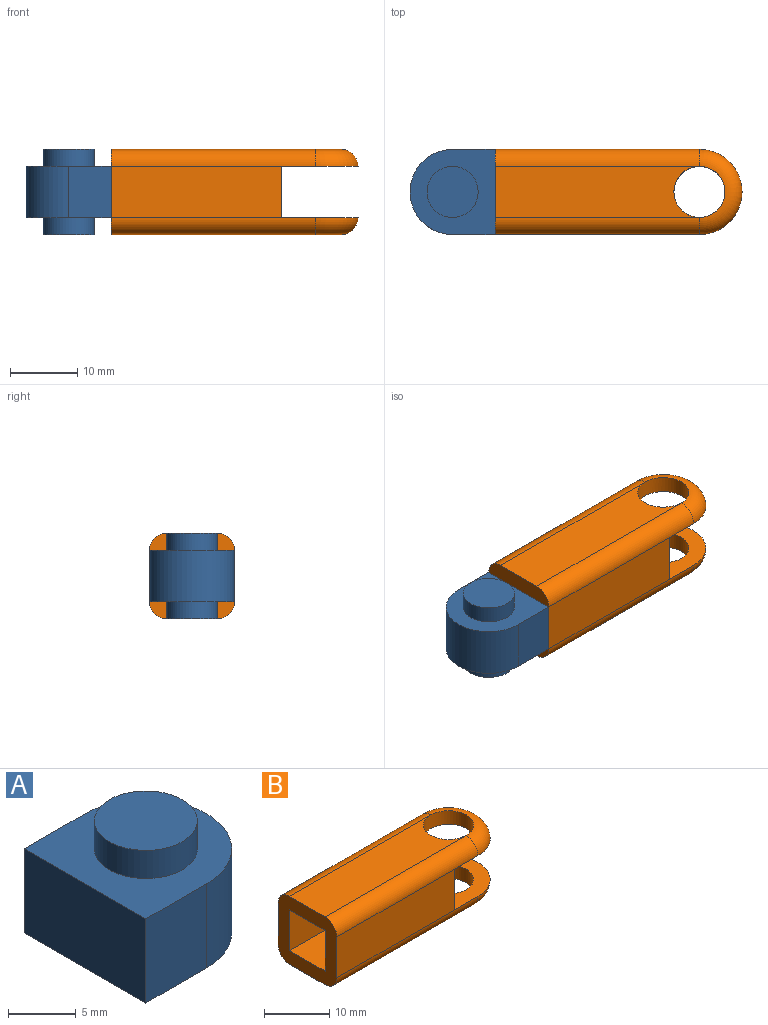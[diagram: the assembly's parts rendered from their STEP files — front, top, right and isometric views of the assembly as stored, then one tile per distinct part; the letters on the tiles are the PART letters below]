
ASSEMBLY  parts=2 mates=1
PART A: 10 faces, bbox 12.7x12.7x12.7 mm
  f0: cylinder r=6.35mm len=12.7mm, axis (0,0,-1), area 152mm2, adj f1,f3,f4,f5
  f1: plane 7.62x6.35mm, normal (0,1,0), area 48.4mm2, adj f0,f2,f4,f5
  f2: plane 12.7x7.62mm, normal (-1,0,0), area 96.8mm2, adj f1,f3,f4,f5
  f3: plane 7.62x6.35mm, normal (0,-1,0), area 48.4mm2, adj f0,f2,f4,f5
  f4: plane 12.7x12.7mm, normal (0,0,1), area 98.4mm2, adj f0,f1,f2,f3,f6
  f5: plane 12.7x12.7mm, normal (0,0,-1), area 98.4mm2, adj f0,f1,f2,f3,f8
  f6: cylinder r=3.81mm len=7.62mm, axis (0,0,-1), area 60.8mm2, adj f4,f7
  f7: plane 7.62x7.62mm, normal (0,0,1), area 45.6mm2, adj f6
  f8: cylinder r=3.81mm len=7.62mm, axis (0,0,1), area 60.8mm2, adj f5,f9
  f9: plane 7.62x7.62mm, normal (0,0,-1), area 45.6mm2, adj f8
PART B: 19 faces, bbox 37.4x13.7x12.7 mm
  f0: plane 7.62x2.54mm, normal (1,0,0), area 19.4mm2, adj f2,f5,f6,f8
  f1: plane 7.62x2.54mm, normal (1,0,0), area 19.4mm2, adj f4,f6,f7,f8
  f2: plane 25.4x7.62mm, normal (0,1,0), area 193.5mm2, adj f0,f10,f14,f16
  f3: plane 30.48x7.62mm, normal (0,0,1), area 209.5mm2, adj f10,f11,f13,f14
  f4: plane 25.4x7.62mm, normal (0,-1,0), area 193.5mm2, adj f1,f10,f13,f17
  f5: plane 25.4x7.62mm, normal (0,-1,0), area 193.5mm2, adj f0,f6,f8,f10
  f6: plane 36.83x12.7mm, normal (0,0,1), area 275.8mm2, adj f0,f1,f5,f7,f10,f12,f16,f17
  f7: plane 25.4x7.62mm, normal (0,1,0), area 193.5mm2, adj f1,f6,f8,f10
  f8: plane 36.83x12.7mm, normal (0,0,-1), area 275.8mm2, adj f0,f1,f5,f7,f10,f11,f13,f14
  f9: plane 30.48x7.62mm, normal (0,0,-1), area 209.5mm2, adj f10,f12,f16,f17
  f10: plane 12.7x12.7mm, normal (-1,0,0), area 97.7mm2, adj f2,f3,f4,f5,f6,f7,f8,f9
  f11: cylinder r=3.81mm len=7.62mm, axis (0,0,1), area 60.8mm2, adj f3,f8,f15
  f12: cylinder r=3.81mm len=7.62mm, axis (0,0,-1), area 60.8mm2, adj f6,f9,f18
  f13: cylinder r=2.54mm len=30.48mm, axis (-1,0,0), area 121.6mm2, adj f3,f4,f8,f10,f15
  f14: cylinder r=2.54mm len=30.48mm, axis (1,0,0), area 121.6mm2, adj f2,f3,f8,f10,f15
  f15: torus R=3.81mm, axis (0,0,-1), area 68mm2, adj f8,f11,f13,f14
  f16: cylinder r=2.54mm len=30.48mm, axis (-1,0,0), area 121.6mm2, adj f2,f6,f9,f10,f18
  f17: cylinder r=2.54mm len=30.48mm, axis (1,0,0), area 121.6mm2, adj f4,f6,f9,f10,f18
  f18: torus R=3.81mm, axis (0,0,-1), area 68mm2, adj f6,f12,f16,f17
PLACE A rot(axis=(0,0,-1),180deg) t=(15.72,-10.85,-21.88)mm
PLACE B t=(22.07,-10.85,-11.72)mm
MATE fastened B.f10 <-> A.f2  axis (-1,0,0) through (22.07,-17.2,-18.07)mm
